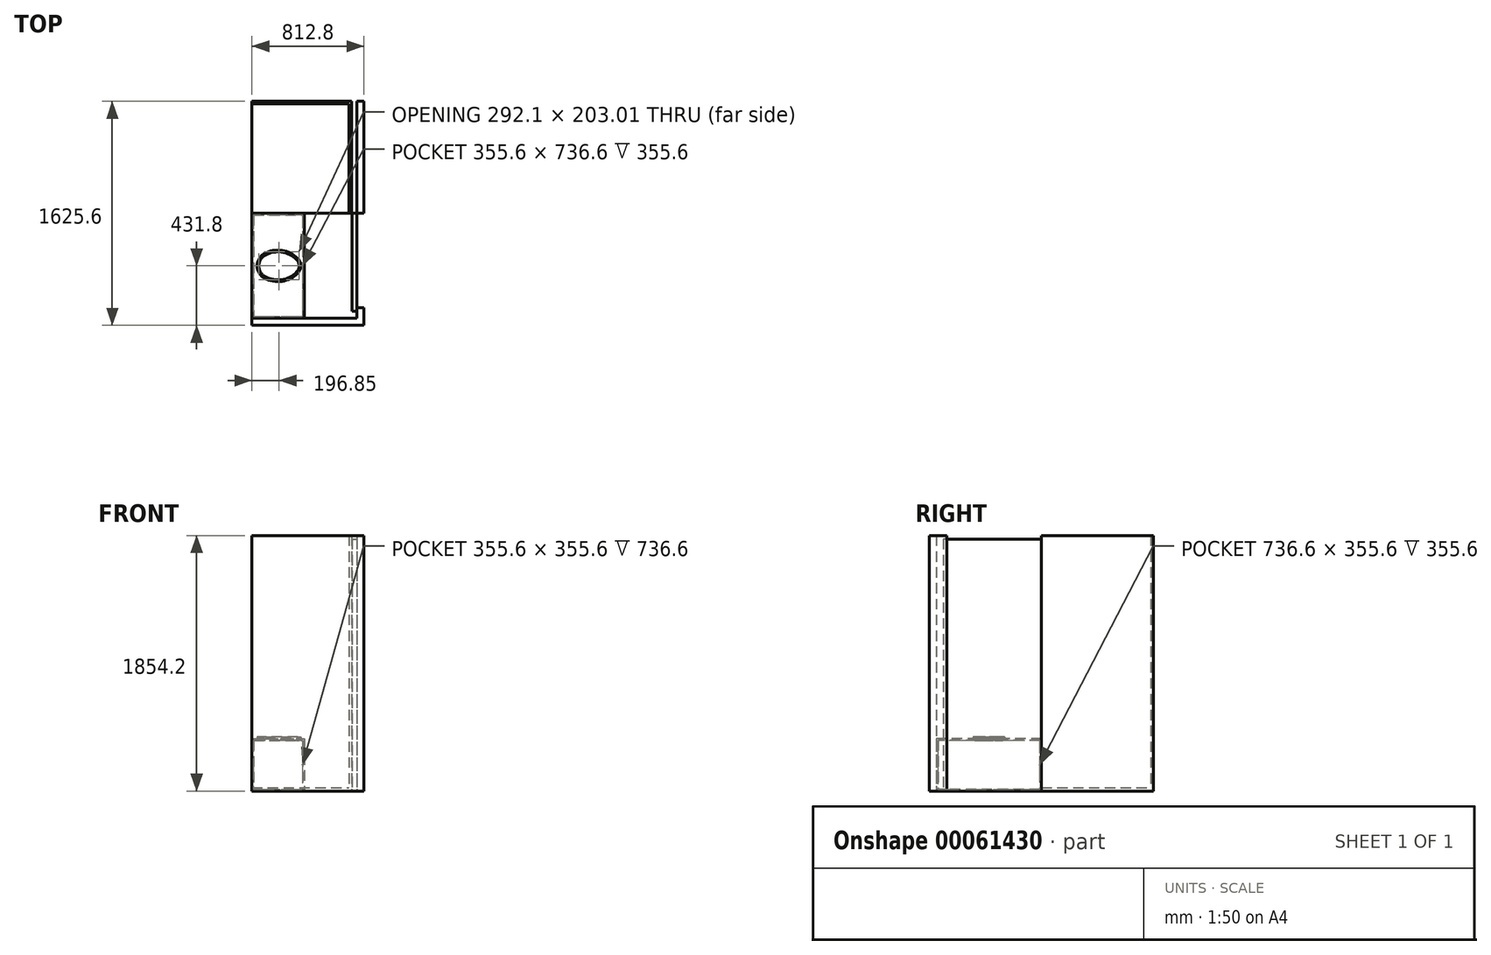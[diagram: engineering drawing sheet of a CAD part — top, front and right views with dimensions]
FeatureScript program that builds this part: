
annotation { "Feature Type Name" : "Feature", "Feature Type Description" : "" }
export const myFeature = defineFeature(function(context is Context, id is Id, definition is map)
    precondition{}
    {
        {
            var Q0;
            Q0=qCreatedBy(makeId("Right.planeOp"),FACE);
            cPlane(context, id + "F0", {"entities" : qUnion([Q0]), "cplaneType" : CPlaneType.OFFSET, "offset" : 812.8 * mm, "width" : 152.4 * mm, "height" : 152.4 * mm});
        }
        {
            var Q0;
            Q0=qCreatedBy(makeId("Top.planeOp"),FACE);
            var sketch = newSketch(context, id + "F1", { "sketchPlane" : qUnion([Q0])});
            skLineSegment(sketch, "E0.bottom", {"start": v(812.8, 0) * mm, "end": v(762, 0) * mm});
            skLineSegment(sketch, "E0.top", {"start": v(812.8, -812.8) * mm, "end": v(762, -812.8) * mm});
            skLineSegment(sketch, "E0.left", {"start": v(812.8, 0) * mm, "end": v(812.8, -812.8) * mm});
            skLineSegment(sketch, "E0.right", {"start": v(762, 0) * mm, "end": v(762, -812.8) * mm});
            skSolve(sketch);
        }
        {
            var Q0;
            Q0 = qSketchRegion(id + "F1", true);
            extrude(context, id + "F2", {"entities" : qUnion([Q0]), "depth" : 1854.2 * mm});
        }
        {
            var Q0;
            Q0=qCreatedBy(makeId("Top.planeOp"),FACE);
            var sketch = newSketch(context, id + "F3", { "sketchPlane" : qUnion([Q0])});
            skLineSegment(sketch, "E1.bottom", {"start": v(0, 0) * mm, "end": v(723.9, 0) * mm});
            skLineSegment(sketch, "E1.top", {"start": v(0, -812.8) * mm, "end": v(723.9, -812.8) * mm});
            skLineSegment(sketch, "E1.left", {"start": v(0, 0) * mm, "end": v(0, -812.8) * mm});
            skLineSegment(sketch, "E1.right", {"start": v(723.9, 0) * mm, "end": v(723.9, -812.8) * mm});
            skSolve(sketch);
        }
        {
            var Q0;
            Q0 = qSketchRegion(id + "F3", true);
            extrude(context, id + "F4", {"entities" : qUnion([Q0]), "depth" : 25.4 * mm});
        }
        {
            var Q0;
            Q0=qCreatedBy(makeId("Top.planeOp"),FACE);
            var sketch = newSketch(context, id + "F5", { "sketchPlane" : qUnion([Q0])});
            skLineSegment(sketch, "E2.bottom", {"start": v(0, -812.8) * mm, "end": v(381, -812.8) * mm});
            skLineSegment(sketch, "E2.top", {"start": v(0, -1574.8) * mm, "end": v(381, -1574.8) * mm});
            skLineSegment(sketch, "E2.left", {"start": v(0, -812.8) * mm, "end": v(0, -1574.8) * mm});
            skLineSegment(sketch, "E2.right", {"start": v(381, -812.8) * mm, "end": v(381, -1574.8) * mm});
            skSolve(sketch);
        }
        {
            var Q0;
            Q0=makeQuery(id+"F5.imprint","IMPRINT",FACE,{"disambiguationData":[TD([[makeQuery(id+"F5.imprint","IMPRINT",EDGE,{"derivedFrom":sQuery(id+"F5.wireOp",EDGE,"E2.bottom")}),-1.0]])]});
            extrude(context, id + "F6", {"entities" : qUnion([Q0]), "depth" : 381 * mm});
        }
        {
            var Q0;
            Q0=qCreatedBy(makeId("Top.planeOp"),FACE);
            var sketch = newSketch(context, id + "F7", { "sketchPlane" : qUnion([Q0])});
            skLineSegment(sketch, "E3", {"start": v(0, -1574.8) * mm, "end": v(762, -1574.8) * mm});
            skLineSegment(sketch, "E4", {"start": v(762, -1574.8) * mm, "end": v(762, -1498.6) * mm});
            skLineSegment(sketch, "E5", {"start": v(762, -1498.6) * mm, "end": v(812.8, -1498.6) * mm});
            skLineSegment(sketch, "E6", {"start": v(812.8, -1498.6) * mm, "end": v(812.8, -1625.6) * mm});
            skLineSegment(sketch, "E7", {"start": v(812.8, -1625.6) * mm, "end": v(0, -1625.6) * mm});
            skLineSegment(sketch, "E8", {"start": v(0, -1625.6) * mm, "end": v(0, -1574.8) * mm});
            skSolve(sketch);
        }
        {
            var Q0;
            Q0=makeQuery(id+"F7.imprint","IMPRINT",FACE,{"disambiguationData":[TD([[makeQuery(id+"F7.imprint","IMPRINT",EDGE,{"derivedFrom":sQuery(id+"F7.wireOp",EDGE,"E3")}),-1.0]])]});
            var Q1;
            Q1=makeQuery(id+"F2.opExtrude","CAP_FACE",FACE,{"disambiguationData":[OSD([sQuery(id+"F1.wireOp",EDGE,"E0.bottom"),sQuery(id+"F1.wireOp",EDGE,"E0.top"),sQuery(id+"F1.wireOp",EDGE,"E0.left"),sQuery(id+"F1.wireOp",EDGE,"E0.right")])],"isStart":false});
            extrude(context, id + "F8", {"entities" : qUnion([Q0]), "endBound" : BoundingType.UP_TO_SURFACE, "endBoundEntityFace" : qUnion([Q1]), "depth" : 25.4 * mm});
        }
        {
            var Q0;
            Q0=makeQuery(id+"F4.opExtrude","CAP_FACE",FACE,{"disambiguationData":[OSD([sQuery(id+"F3.wireOp",EDGE,"E1.bottom"),sQuery(id+"F3.wireOp",EDGE,"E1.top"),sQuery(id+"F3.wireOp",EDGE,"E1.left"),sQuery(id+"F3.wireOp",EDGE,"E1.right")])],"isStart":false});
            var sketch = newSketch(context, id + "F9", { "sketchPlane" : qUnion([Q0])});
            skLineSegment(sketch, "E9", {"start": v(0, -19.05) * mm, "end": v(0, 0) * mm});
            skLineSegment(sketch, "E10", {"start": v(0, 0) * mm, "end": v(723.9, 0) * mm});
            skLineSegment(sketch, "E11", {"start": v(723.9, 0) * mm, "end": v(723.9, -812.8) * mm});
            skLineSegment(sketch, "E12", {"start": v(723.9, -812.8) * mm, "end": v(704.85, -812.8) * mm});
            skLineSegment(sketch, "E13", {"start": v(704.85, -812.8) * mm, "end": v(704.85, -19.05) * mm});
            skLineSegment(sketch, "E14", {"start": v(704.85, -19.05) * mm, "end": v(0, -19.05) * mm});
            skSolve(sketch);
        }
        {
            var Q0;
            Q0=makeQuery(id+"F9.imprint","IMPRINT",FACE,{"disambiguationData":[TD([[makeQuery(id+"F9.imprint","IMPRINT",EDGE,{"derivedFrom":sQuery(id+"F9.wireOp",EDGE,"E9")}),1.0]])]});
            var Q1;
            Q1=makeQuery(id+"F2.opExtrude","CAP_FACE",FACE,{"disambiguationData":[OSD([sQuery(id+"F1.wireOp",EDGE,"E0.bottom"),sQuery(id+"F1.wireOp",EDGE,"E0.top"),sQuery(id+"F1.wireOp",EDGE,"E0.left"),sQuery(id+"F1.wireOp",EDGE,"E0.right")])],"isStart":false});
            extrude(context, id + "F10", {"entities" : qUnion([Q0]), "operationType" : NewBodyOperationType.ADD, "endBound" : BoundingType.UP_TO_SURFACE, "endBoundEntityFace" : qUnion([Q1]), "depth" : 25.4 * mm});
        }
        {
            var Q0;
            Q0=qCreatedBy(makeId("Top.planeOp"),FACE);
            var sketch = newSketch(context, id + "F11", { "sketchPlane" : qUnion([Q0])});
            skLineSegment(sketch, "E15.bottom", {"start": v(727.08, -812.8) * mm, "end": v(762, -812.8) * mm});
            skLineSegment(sketch, "E15.top", {"start": v(727.08, -1524) * mm, "end": v(762, -1524) * mm});
            skLineSegment(sketch, "E15.left", {"start": v(727.08, -812.8) * mm, "end": v(727.08, -1524) * mm});
            skLineSegment(sketch, "E15.right", {"start": v(762, -812.8) * mm, "end": v(762, -1524) * mm});
            skSolve(sketch);
        }
        {
            var Q0;
            Q0=makeQuery(id+"F11.imprint","IMPRINT",FACE,{"disambiguationData":[TD([[makeQuery(id+"F11.imprint","IMPRINT",EDGE,{"derivedFrom":sQuery(id+"F11.wireOp",EDGE,"E15.bottom")}),-1.0]])]});
            extrude(context, id + "F12", {"entities" : qUnion([Q0]), "depth" : 1828.8 * mm});
        }
        {
            var Q0;
            Q0=makeQuery(id+"F6.opExtrude","CAP_FACE",FACE,{"disambiguationData":[OSD([sQuery(id+"F5.wireOp",EDGE,"E2.bottom"),sQuery(id+"F5.wireOp",EDGE,"E2.top"),sQuery(id+"F5.wireOp",EDGE,"E2.left"),sQuery(id+"F5.wireOp",EDGE,"E2.right")])],"isStart":false});
            var sketch = newSketch(context, id + "F13", { "sketchPlane" : qUnion([Q0])});
            skArc(sketch, "E16", {"start": v(333.78, -1140.42) * mm, "mid": v(218.2, -1081.7) * mm, "end": v(90.63, -1104.83) * mm});
            skArc(sketch, "E17", {"start": v(333.78, -1247.18) * mm, "mid": v(355.6, -1193.8) * mm, "end": v(333.78, -1140.42) * mm});
            skArc(sketch, "E18", {"start": v(90.63, -1104.83) * mm, "mid": v(38.1, -1193.8) * mm, "end": v(90.63, -1282.77) * mm});
            skArc(sketch, "E19", {"start": v(90.63, -1282.77) * mm, "mid": v(218.2, -1305.9) * mm, "end": v(333.78, -1247.18) * mm});
            skLineSegment(sketch, "E20", {"start": v(0, -1193.8) * mm, "end": v(139.7, -1193.8) * mm, "construction": true});
            skLineSegment(sketch, "E21", {"start": v(279.4, -1193.8) * mm, "end": v(381, -1193.8) * mm, "construction": true});
            skSolve(sketch);
        }
        {
            var Q0;
            Q0=makeQuery(id+"F13.imprint","IMPRINT",FACE,{"disambiguationData":[TD([[makeQuery(id+"F13.imprint","IMPRINT",EDGE,{"derivedFrom":sQuery(id+"F13.wireOp",EDGE,"E16")}),1.0]])]});
            extrude(context, id + "F14", {"entities" : qUnion([Q0]), "operationType" : NewBodyOperationType.ADD, "depth" : 12.7 * mm});
        }
        {
            var Q0;
            Q0=makeQuery(id+"F14.opExtrude","CAP_FACE",FACE,{"disambiguationData":[OSD([sQuery(id+"F13.wireOp",EDGE,"E16"),sQuery(id+"F13.wireOp",EDGE,"E17"),sQuery(id+"F13.wireOp",EDGE,"E18"),sQuery(id+"F13.wireOp",EDGE,"E19")])],"isStart":false});
            shell(context, id + "F15", {"entities" : qUnion([Q0]), "thickness" : 12.7 * mm});
        }
    });
